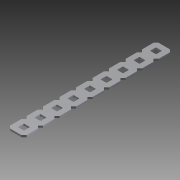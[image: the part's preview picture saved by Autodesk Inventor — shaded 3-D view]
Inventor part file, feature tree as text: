
AUTODESK INVENTOR PART (.ipt)
format: ipt  version: 2014 (Build 180170000, 170)  size: 544,256 bytes
history: native  units: in
note: dims shown in document units (in); Inventor stores cm internally (conversion verified against a paired STEP export)
features: other x1, imported_body x1, extrude x1, sketch x1
ambient origin geometry x8: Origin, YZ Plane, XZ Plane, XY Plane, X Axis, Y Axis, Z Axis, Center Point
bodies: Body1 (feature_tree)
feature tree (4):
  parser-record x1  (decoder bookkeeping rows leaked as tree rows — omitted from the tree; the rows remain in map.json)
  imported_body  "Base1"
  extrude  "Extrusion1"  [1 undecoded]
  sketch  "Sketch1"  dims[d0=1.0in d1=0.0in]
note: 1 required parameter value undecoded (feature->parameter linkage not recoverable at this tier; creation-order binding heuristic only, values carry confidence <= 0.55)
